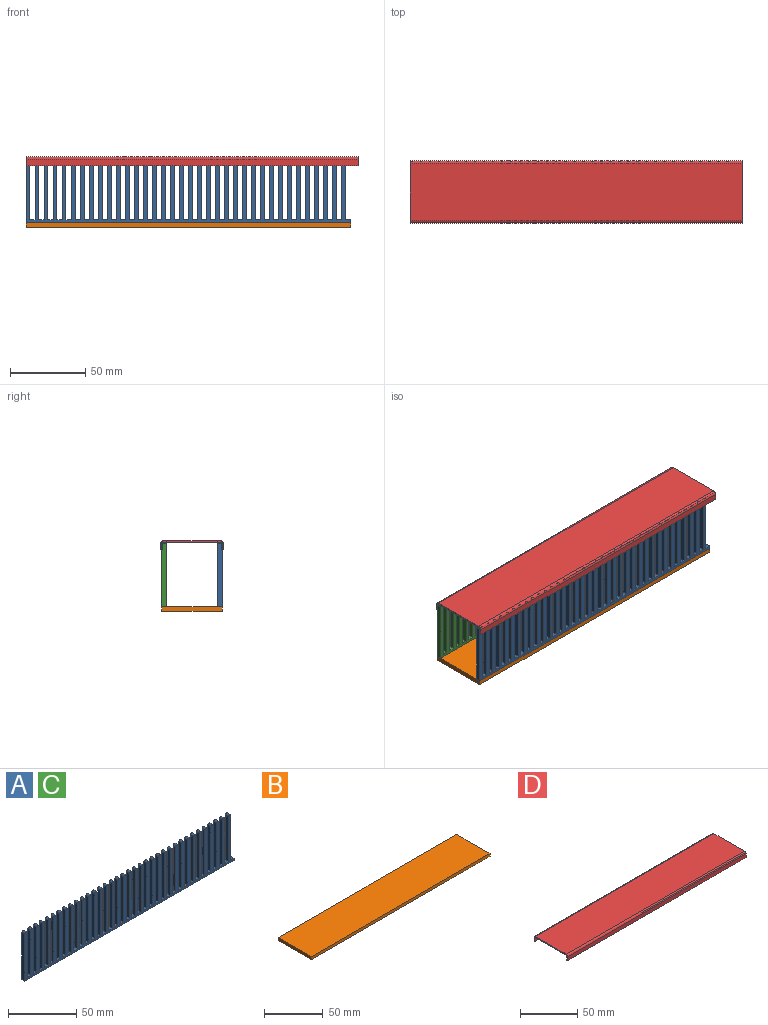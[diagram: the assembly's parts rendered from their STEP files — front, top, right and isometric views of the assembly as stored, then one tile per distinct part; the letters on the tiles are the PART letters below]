
ASSEMBLY  parts=4 mates=3
PART A: 148 faces, bbox 216x3x43.3 mm
  f0: plane 3.4x3mm, normal (0,0,1), area 10.2mm2, adj f1,f5,f6,f10
  f1: plane 40x3mm, normal (1,0,0), area 120mm2, adj f0,f2,f5,f6
  f2: cylinder r=1.3mm len=3mm, axis (0,1,0), area 12.2mm2, adj f1,f3,f5,f6
  f3: plane 42x3mm, normal (-1,0,0), area 126mm2, adj f2,f4,f5,f6
  f4: plane 216x3mm, normal (0,0,-1), area 648mm2, adj f3,f5,f6,f128
  f5: plane 216x43.3mm, normal (0,-1,0), area 4267.6mm2, adj f0,f1,f2,f3,f4,f7,f8,f9
  f6: plane 216x43.3mm, normal (0,1,0), area 4267.6mm2, adj f0,f1,f2,f3,f4,f7,f8,f9
  f7: plane 3.4x3mm, normal (0,0,1), area 10.2mm2, adj f5,f6,f8,f14
  f8: plane 40x3mm, normal (1,0,0), area 120mm2, adj f5,f6,f7,f9
  f9: cylinder r=1.3mm len=3mm, axis (0,1,0), area 12.2mm2, adj f5,f6,f8,f10
  f10: plane 40x3mm, normal (-1,0,0), area 120mm2, adj f0,f5,f6,f9
  f11: plane 3.4x3mm, normal (0,0,1), area 10.2mm2, adj f5,f6,f12,f18
  f12: plane 40x3mm, normal (1,0,0), area 120mm2, adj f5,f6,f11,f13
  f13: cylinder r=1.3mm len=3mm, axis (0,1,0), area 12.2mm2, adj f5,f6,f12,f14
  f14: plane 40x3mm, normal (-1,0,0), area 120mm2, adj f5,f6,f7,f13
  f15: plane 3.4x3mm, normal (0,0,1), area 10.2mm2, adj f5,f6,f16,f22
  f16: plane 40x3mm, normal (1,0,0), area 120mm2, adj f5,f6,f15,f17
  f17: cylinder r=1.3mm len=3mm, axis (0,1,0), area 12.2mm2, adj f5,f6,f16,f18
  f18: plane 40x3mm, normal (-1,0,0), area 120mm2, adj f5,f6,f11,f17
  f19: plane 3.4x3mm, normal (0,0,1), area 10.2mm2, adj f5,f6,f20,f26
  f20: plane 40x3mm, normal (1,0,0), area 120mm2, adj f5,f6,f19,f21
  f21: cylinder r=1.3mm len=3mm, axis (0,1,0), area 12.2mm2, adj f5,f6,f20,f22
  f22: plane 40x3mm, normal (-1,0,0), area 120mm2, adj f5,f6,f15,f21
  f23: plane 3.4x3mm, normal (0,0,1), area 10.2mm2, adj f5,f6,f24,f30
  f24: plane 40x3mm, normal (1,0,0), area 120mm2, adj f5,f6,f23,f25
  f25: cylinder r=1.3mm len=3mm, axis (0,1,0), area 12.2mm2, adj f5,f6,f24,f26
  f26: plane 40x3mm, normal (-1,0,0), area 120mm2, adj f5,f6,f19,f25
  f27: plane 3.4x3mm, normal (0,0,1), area 10.2mm2, adj f5,f6,f28,f34
  f28: plane 40x3mm, normal (1,0,0), area 120mm2, adj f5,f6,f27,f29
  f29: cylinder r=1.3mm len=3mm, axis (0,1,0), area 12.2mm2, adj f5,f6,f28,f30
  f30: plane 40x3mm, normal (-1,0,0), area 120mm2, adj f5,f6,f23,f29
  f31: plane 3.4x3mm, normal (0,0,1), area 10.2mm2, adj f5,f6,f32,f38
  f32: plane 40x3mm, normal (1,0,0), area 120mm2, adj f5,f6,f31,f33
  f33: cylinder r=1.3mm len=3mm, axis (0,1,0), area 12.2mm2, adj f5,f6,f32,f34
  f34: plane 40x3mm, normal (-1,0,0), area 120mm2, adj f5,f6,f27,f33
  f35: plane 3.4x3mm, normal (0,0,1), area 10.2mm2, adj f5,f6,f36,f42
  f36: plane 40x3mm, normal (1,0,0), area 120mm2, adj f5,f6,f35,f37
  f37: cylinder r=1.3mm len=3mm, axis (0,1,0), area 12.2mm2, adj f5,f6,f36,f38
  f38: plane 40x3mm, normal (-1,0,0), area 120mm2, adj f5,f6,f31,f37
  f39: plane 3.4x3mm, normal (0,0,1), area 10.2mm2, adj f5,f6,f40,f46
  f40: plane 40x3mm, normal (1,0,0), area 120mm2, adj f5,f6,f39,f41
  f41: cylinder r=1.3mm len=3mm, axis (0,1,0), area 12.2mm2, adj f5,f6,f40,f42
  f42: plane 40x3mm, normal (-1,0,0), area 120mm2, adj f5,f6,f35,f41
  f43: plane 3.4x3mm, normal (0,0,1), area 10.2mm2, adj f5,f6,f44,f50
  f44: plane 40x3mm, normal (1,0,0), area 120mm2, adj f5,f6,f43,f45
  f45: cylinder r=1.3mm len=3mm, axis (0,1,0), area 12.2mm2, adj f5,f6,f44,f46
  f46: plane 40x3mm, normal (-1,0,0), area 120mm2, adj f5,f6,f39,f45
  f47: plane 3.4x3mm, normal (0,0,1), area 10.2mm2, adj f5,f6,f48,f54
  f48: plane 40x3mm, normal (1,0,0), area 120mm2, adj f5,f6,f47,f49
  f49: cylinder r=1.3mm len=3mm, axis (0,1,0), area 12.2mm2, adj f5,f6,f48,f50
  f50: plane 40x3mm, normal (-1,0,0), area 120mm2, adj f5,f6,f43,f49
  f51: plane 3.4x3mm, normal (0,0,1), area 10.2mm2, adj f5,f6,f52,f58
  f52: plane 40x3mm, normal (1,0,0), area 120mm2, adj f5,f6,f51,f53
  f53: cylinder r=1.3mm len=3mm, axis (0,1,0), area 12.2mm2, adj f5,f6,f52,f54
  f54: plane 40x3mm, normal (-1,0,0), area 120mm2, adj f5,f6,f47,f53
  f55: plane 3.4x3mm, normal (0,0,1), area 10.2mm2, adj f5,f6,f56,f62
  f56: plane 40x3mm, normal (1,0,0), area 120mm2, adj f5,f6,f55,f57
  f57: cylinder r=1.3mm len=3mm, axis (0,1,0), area 12.2mm2, adj f5,f6,f56,f58
  f58: plane 40x3mm, normal (-1,0,0), area 120mm2, adj f5,f6,f51,f57
  f59: plane 3.4x3mm, normal (0,0,1), area 10.2mm2, adj f5,f6,f60,f66
  f60: plane 40x3mm, normal (1,0,0), area 120mm2, adj f5,f6,f59,f61
  f61: cylinder r=1.3mm len=3mm, axis (0,1,0), area 12.2mm2, adj f5,f6,f60,f62
  f62: plane 40x3mm, normal (-1,0,0), area 120mm2, adj f5,f6,f55,f61
  f63: plane 3.4x3mm, normal (0,0,1), area 10.2mm2, adj f5,f6,f64,f70
  f64: plane 40x3mm, normal (1,0,0), area 120mm2, adj f5,f6,f63,f65
  f65: cylinder r=1.3mm len=3mm, axis (0,1,0), area 12.2mm2, adj f5,f6,f64,f66
  f66: plane 40x3mm, normal (-1,0,0), area 120mm2, adj f5,f6,f59,f65
  f67: plane 3.4x3mm, normal (0,0,1), area 10.2mm2, adj f5,f6,f68,f74
  f68: plane 40x3mm, normal (1,0,0), area 120mm2, adj f5,f6,f67,f69
  f69: cylinder r=1.3mm len=3mm, axis (0,1,0), area 12.2mm2, adj f5,f6,f68,f70
  f70: plane 40x3mm, normal (-1,0,0), area 120mm2, adj f5,f6,f63,f69
  f71: plane 3.4x3mm, normal (0,0,1), area 10.2mm2, adj f5,f6,f72,f78
  f72: plane 40x3mm, normal (1,0,0), area 120mm2, adj f5,f6,f71,f73
  f73: cylinder r=1.3mm len=3mm, axis (0,1,0), area 12.2mm2, adj f5,f6,f72,f74
  f74: plane 40x3mm, normal (-1,0,0), area 120mm2, adj f5,f6,f67,f73
  f75: plane 3.4x3mm, normal (0,0,1), area 10.2mm2, adj f5,f6,f76,f82
  f76: plane 40x3mm, normal (1,0,0), area 120mm2, adj f5,f6,f75,f77
  f77: cylinder r=1.3mm len=3mm, axis (0,1,0), area 12.2mm2, adj f5,f6,f76,f78
  f78: plane 40x3mm, normal (-1,0,0), area 120mm2, adj f5,f6,f71,f77
  f79: plane 3.4x3mm, normal (0,0,1), area 10.2mm2, adj f5,f6,f80,f86
  f80: plane 40x3mm, normal (1,0,0), area 120mm2, adj f5,f6,f79,f81
  f81: cylinder r=1.3mm len=3mm, axis (0,1,0), area 12.2mm2, adj f5,f6,f80,f82
  f82: plane 40x3mm, normal (-1,0,0), area 120mm2, adj f5,f6,f75,f81
  f83: plane 3.4x3mm, normal (0,0,1), area 10.2mm2, adj f5,f6,f84,f90
  f84: plane 40x3mm, normal (1,0,0), area 120mm2, adj f5,f6,f83,f85
  f85: cylinder r=1.3mm len=3mm, axis (0,1,0), area 12.2mm2, adj f5,f6,f84,f86
  f86: plane 40x3mm, normal (-1,0,0), area 120mm2, adj f5,f6,f79,f85
  f87: plane 3.4x3mm, normal (0,0,1), area 10.2mm2, adj f5,f6,f88,f94
  f88: plane 40x3mm, normal (1,0,0), area 120mm2, adj f5,f6,f87,f89
  f89: cylinder r=1.3mm len=3mm, axis (0,1,0), area 12.2mm2, adj f5,f6,f88,f90
  f90: plane 40x3mm, normal (-1,0,0), area 120mm2, adj f5,f6,f83,f89
  f91: plane 3.4x3mm, normal (0,0,1), area 10.2mm2, adj f5,f6,f92,f98
  f92: plane 40x3mm, normal (1,0,0), area 120mm2, adj f5,f6,f91,f93
  f93: cylinder r=1.3mm len=3mm, axis (0,1,0), area 12.2mm2, adj f5,f6,f92,f94
  f94: plane 40x3mm, normal (-1,0,0), area 120mm2, adj f5,f6,f87,f93
  f95: plane 3.4x3mm, normal (0,0,1), area 10.2mm2, adj f5,f6,f96,f102
  f96: plane 40x3mm, normal (1,0,0), area 120mm2, adj f5,f6,f95,f97
  f97: cylinder r=1.3mm len=3mm, axis (0,1,0), area 12.2mm2, adj f5,f6,f96,f98
  f98: plane 40x3mm, normal (-1,0,0), area 120mm2, adj f5,f6,f91,f97
  f99: plane 3.4x3mm, normal (0,0,1), area 10.2mm2, adj f5,f6,f100,f106
  f100: plane 40x3mm, normal (1,0,0), area 120mm2, adj f5,f6,f99,f101
  f101: cylinder r=1.3mm len=3mm, axis (0,1,0), area 12.2mm2, adj f5,f6,f100,f102
  f102: plane 40x3mm, normal (-1,0,0), area 120mm2, adj f5,f6,f95,f101
  f103: plane 3.4x3mm, normal (0,0,1), area 10.2mm2, adj f5,f6,f104,f110
  f104: plane 40x3mm, normal (1,0,0), area 120mm2, adj f5,f6,f103,f105
  f105: cylinder r=1.3mm len=3mm, axis (0,1,0), area 12.2mm2, adj f5,f6,f104,f106
  f106: plane 40x3mm, normal (-1,0,0), area 120mm2, adj f5,f6,f99,f105
  f107: plane 3.4x3mm, normal (0,0,1), area 10.2mm2, adj f5,f6,f108,f114
  f108: plane 40x3mm, normal (1,0,0), area 120mm2, adj f5,f6,f107,f109
  f109: cylinder r=1.3mm len=3mm, axis (0,1,0), area 12.2mm2, adj f5,f6,f108,f110
  f110: plane 40x3mm, normal (-1,0,0), area 120mm2, adj f5,f6,f103,f109
  f111: plane 3.4x3mm, normal (0,0,1), area 10.2mm2, adj f5,f6,f112,f118
  f112: plane 40x3mm, normal (1,0,0), area 120mm2, adj f5,f6,f111,f113
  f113: cylinder r=1.3mm len=3mm, axis (0,1,0), area 12.2mm2, adj f5,f6,f112,f114
  f114: plane 40x3mm, normal (-1,0,0), area 120mm2, adj f5,f6,f107,f113
  f115: plane 3.4x3mm, normal (0,0,1), area 10.2mm2, adj f5,f6,f116,f122
  f116: plane 40x3mm, normal (1,0,0), area 120mm2, adj f5,f6,f115,f117
  f117: cylinder r=1.3mm len=3mm, axis (0,1,0), area 12.2mm2, adj f5,f6,f116,f118
  f118: plane 40x3mm, normal (-1,0,0), area 120mm2, adj f5,f6,f111,f117
  f119: plane 3.4x3mm, normal (0,0,1), area 10.2mm2, adj f5,f6,f120,f126
  f120: plane 40x3mm, normal (1,0,0), area 120mm2, adj f5,f6,f119,f121
  f121: cylinder r=1.3mm len=3mm, axis (0,1,0), area 12.2mm2, adj f5,f6,f120,f122
  f122: plane 40x3mm, normal (-1,0,0), area 120mm2, adj f5,f6,f115,f121
  f123: plane 3.4x3mm, normal (0,0,1), area 10.2mm2, adj f5,f6,f124,f135
  f124: plane 40x3mm, normal (1,0,0), area 120mm2, adj f5,f6,f123,f125
  f125: cylinder r=1.3mm len=3mm, axis (0,1,0), area 12.2mm2, adj f5,f6,f124,f126
  f126: plane 40x3mm, normal (-1,0,0), area 120mm2, adj f5,f6,f119,f125
  f127: plane 40x3mm, normal (-1,0,0), area 120mm2, adj f5,f6,f131,f144
  f128: plane 3x2mm, normal (1,0,0), area 6mm2, adj f4,f5,f6,f129
  f129: plane 3.4x3mm, normal (0,0,1), area 10.2mm2, adj f5,f6,f128,f130
  f130: plane 40x3mm, normal (1,0,0), area 120mm2, adj f5,f6,f129,f131
  f131: cylinder r=1.3mm len=3mm, axis (0,1,0), area 12.2mm2, adj f5,f6,f127,f130
  f132: plane 3.4x3mm, normal (0,0,1), area 10.2mm2, adj f5,f6,f133,f143
  f133: plane 40x3mm, normal (1,0,0), area 120mm2, adj f5,f6,f132,f134
  f134: cylinder r=1.3mm len=3mm, axis (0,1,0), area 12.2mm2, adj f5,f6,f133,f135
  f135: plane 40x3mm, normal (-1,0,0), area 120mm2, adj f5,f6,f123,f134
  f136: plane 40x3mm, normal (-1,0,0), area 120mm2, adj f5,f6,f139,f140
  f137: plane 3.4x3mm, normal (0,0,1), area 10.2mm2, adj f5,f6,f138,f147
  f138: plane 40x3mm, normal (1,0,0), area 120mm2, adj f5,f6,f137,f139
  f139: cylinder r=1.3mm len=3mm, axis (0,1,0), area 12.2mm2, adj f5,f6,f136,f138
  f140: plane 3.4x3mm, normal (0,0,1), area 10.2mm2, adj f5,f6,f136,f141
  f141: plane 40x3mm, normal (1,0,0), area 120mm2, adj f5,f6,f140,f142
  f142: cylinder r=1.3mm len=3mm, axis (0,1,0), area 12.2mm2, adj f5,f6,f141,f143
  f143: plane 40x3mm, normal (-1,0,0), area 120mm2, adj f5,f6,f132,f142
  f144: plane 3.4x3mm, normal (0,0,1), area 10.2mm2, adj f5,f6,f127,f145
  f145: plane 40x3mm, normal (1,0,0), area 120mm2, adj f5,f6,f144,f146
  f146: cylinder r=1.3mm len=3mm, axis (0,1,0), area 12.2mm2, adj f5,f6,f145,f147
  f147: plane 40x3mm, normal (-1,0,0), area 120mm2, adj f5,f6,f137,f146
PART B: 6 faces, bbox 216x40x3 mm
  f0: plane 216x3mm, normal (0,1,0), area 648mm2, adj f1,f3,f4,f5
  f1: plane 40x3mm, normal (-1,0,0), area 120mm2, adj f0,f2,f4,f5
  f2: plane 216x3mm, normal (0,-1,0), area 648mm2, adj f1,f3,f4,f5
  f3: plane 40x3mm, normal (1,0,0), area 120mm2, adj f0,f2,f4,f5
  f4: plane 216x40mm, normal (0,0,1), area 8640mm2, adj f0,f1,f2,f3
  f5: plane 216x40mm, normal (0,0,-1), area 8640mm2, adj f0,f1,f2,f3
PART C: same geometry as A
PART D: 12 faces, bbox 220.8x41.7x6 mm
  f0: plane 220.82x1mm, normal (0,0,-1), area 220.8mm2, adj f1,f4,f5,f8
  f1: plane 41.7x6mm, normal (-1,0,0), area 50mm2, adj f0,f2,f3,f4,f6,f7,f8,f9
  f2: plane 220.82x1mm, normal (0,0,-1), area 220.8mm2, adj f1,f3,f5,f7
  f3: plane 220.82x4mm, normal (0,1,0), area 883.3mm2, adj f1,f2,f5,f11
  f4: plane 220.82x4mm, normal (0,-1,0), area 883.3mm2, adj f0,f1,f5,f10
  f5: plane 41.7x6mm, normal (1,0,0), area 50mm2, adj f0,f2,f3,f4,f6,f7,f8,f9
  f6: plane 220.82x37.7mm, normal (0,0,1), area 8324mm2, adj f1,f5,f10,f11
  f7: plane 220.82x5mm, normal (0,-1,0), area 1104.1mm2, adj f1,f2,f5,f9
  f8: plane 220.82x5mm, normal (0,1,0), area 1104.1mm2, adj f0,f1,f5,f9
  f9: plane 220.82x39.7mm, normal (0,0,-1), area 8765.6mm2, adj f1,f5,f7,f8
  f10: cylinder r=2mm len=220.82mm, axis (-1,0,0), area 693.7mm2, adj f1,f4,f5,f6
  f11: cylinder r=2mm len=220.82mm, axis (1,0,0), area 693.7mm2, adj f1,f3,f5,f6
PLACE A t=(-75.24,4.55,-120.58)mm
PLACE B t=(-75.24,44.55,-136.55)mm
PLACE C t=(-75.24,41.55,-120.58)mm
PLACE D t=(-72.5,88.1,-95.55)mm
MATE fastened C.f4 <-> B.f4  axis (0,0,-1) through (-77.69,-8.45,-133.55)mm
MATE slider D.f1 <-> B.f1  axis (-1,0,0) through (-77.69,-28.45,-90.55)mm
MATE fastened A.f4 <-> B.f4  axis (0,0,-1) through (-77.69,-48.45,-133.55)mm
